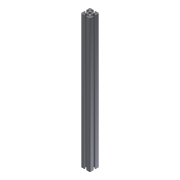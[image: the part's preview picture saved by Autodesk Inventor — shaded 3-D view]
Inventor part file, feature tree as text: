
AUTODESK INVENTOR PART (.ipt)
format: ipt  version: 2016 (Build 200138000, 138)  size: 182,272 bytes
history: native  units: mm
features: other x42, sketch x5, hole x4, extrude x1
ambient origin geometry x8: Origin, YZ Plane, XZ Plane, XY Plane, X Axis, Y Axis, Z Axis, Center Point
bodies: Solid1 (feature_tree)
feature tree (52):
  extrude  "Extrusion1"  [1 undecoded]
  hole  "Drilling 1"  [1 undecoded]
  hole  "Drilling 2"  [1 undecoded]
  hole  "Drilling 3"  [1 undecoded]
  hole  "Drilling 4"  [1 undecoded]
  other  "side_4d_XY"
  other  "side_4d_YZ"
  other  "side_4d_ZX"
  other  "side_4d_X"
  other  "side_4d_Y"
  other  "side_4d_Z"
  other  "side_4d_Center"
  other  "side_1a_XY"
  other  "side_1a_YZ"
  other  "side_1a_ZX"
  other  "side_1a_X"
  other  "side_1a_Y"
  other  "side_1a_Z"
  other  "side_1a_Center"
  other  "side_2b_XY"
  other  "side_2b_YZ"
  other  "side_2b_ZX"
  other  "side_2b_X"
  other  "side_2b_Y"
  other  "side_2b_Z"
  other  "side_2b_Center"
  other  "side_3c_XY"
  other  "side_3c_YZ"
  other  "side_3c_ZX"
  other  "side_3c_X"
  other  "side_3c_Y"
  other  "side_3c_Z"
  other  "side_3c_Center"
  other  "end_XY"
  other  "end_YZ"
  other  "end_ZX"
  other  "end_X"
  other  "end_Y"
  other  "end_Z"
  other  "end_Center"
  other  "start_XY"
  other  "start_YZ"
  other  "start_ZX"
  other  "start_X"
  other  "start_Y"
  other  "start_Z"
  other  "start_Center"
  sketch  "Skizze_1"  dims[d0=587.0mm d1=0.0mm]
  sketch  "Sketch2"  dims[d2=5.0mm d3=6.0mm d4=4.0mm d5=2.0mm d6=90.0deg d7=6000.0mm d8=0.0mm]
  sketch  "Sketch3"  dims[d9=5.0mm d10=6.0mm d11=4.0mm d12=2.0mm d13=90.0deg d14=6000.0mm d15=0.0mm]
  sketch  "Sketch4"  dims[d16=5.0mm d17=6.0mm d18=4.0mm d19=2.0mm d20=90.0deg d21=6000.0mm d22=0.0mm]
  sketch  "Sketch5"  dims[d23=5.0mm d24=6.0mm d25=4.0mm d26=2.0mm d27=90.0deg d28=6000.0mm d29=0.0mm]
note: 5 required parameter values undecoded (feature->parameter linkage not recoverable at this tier; creation-order binding heuristic only, values carry confidence <= 0.55)
